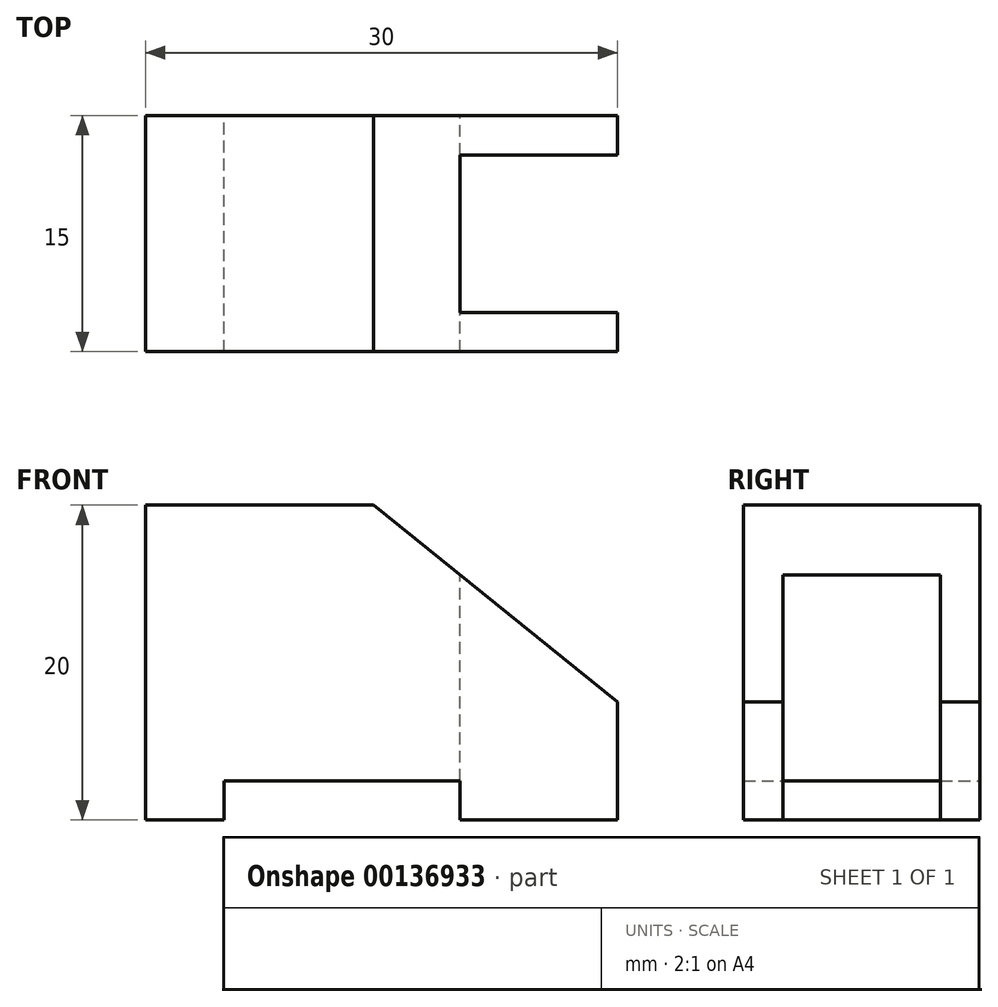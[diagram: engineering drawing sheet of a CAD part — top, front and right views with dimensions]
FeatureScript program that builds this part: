
annotation { "Feature Type Name" : "Feature", "Feature Type Description" : "" }
export const myFeature = defineFeature(function(context is Context, id is Id, definition is map)
    precondition{}
    {
        {
            var Q0;
            Q0=qCreatedBy(makeId("Front.planeOp"),FACE);
            var sketch = newSketch(context, id + "F0", { "sketchPlane" : qUnion([Q0])});
            skLineSegment(sketch, "E0.bottom", {"start": v(0, 0) * mm, "end": v(30, 0) * mm});
            skLineSegment(sketch, "E0.top", {"start": v(0, 20) * mm, "end": v(30, 20) * mm});
            skLineSegment(sketch, "E0.left", {"start": v(0, 0) * mm, "end": v(0, 20) * mm});
            skLineSegment(sketch, "E0.right", {"start": v(30, 0) * mm, "end": v(30, 20) * mm});
            skLineSegment(sketch, "E1", {"start": v(14.5, 20) * mm, "end": v(30, 7.5) * mm});
            skLineSegment(sketch, "E2.bottom", {"start": v(5, 0) * mm, "end": v(20, 0) * mm});
            skLineSegment(sketch, "E2.top", {"start": v(5, 2.5) * mm, "end": v(20, 2.5) * mm});
            skLineSegment(sketch, "E2.left", {"start": v(5, 0) * mm, "end": v(5, 2.5) * mm});
            skLineSegment(sketch, "E2.right", {"start": v(20, 0) * mm, "end": v(20, 2.5) * mm});
            skSolve(sketch);
        }
        {
            var Q0;
            {var subQ0=sQuery(id+"F0.wireOp",EDGE,"E0.left");Q0=makeQuery(id+"F0.imprint","IMPRINT",FACE,{"disambiguationData":[TD([[makeQuery(id+"F0.imprint","IMPRINT",EDGE,{"derivedFrom":subQ0}),-1.0]])]});}
            extrude(context, id + "F1", {"entities" : qUnion([Q0]), "endBound" : BoundingType.SYMMETRIC, "depth" : 15 * mm});
        }
        {
            var Q0;
            Q0=makeQuery(id+"F1.opExtrude","SWEPT_FACE",FACE,{"disambiguationData":[OSD([sQuery(id+"F0.wireOp",EDGE,"E0.top")])]});
            var sketch = newSketch(context, id + "F2", { "sketchPlane" : qUnion([Q0])});
            skLineSegment(sketch, "E3.bottom", {"start": v(20, -5) * mm, "end": v(30, -5) * mm});
            skLineSegment(sketch, "E3.top", {"start": v(20, 5) * mm, "end": v(30, 5) * mm});
            skLineSegment(sketch, "E3.left", {"start": v(20, -5) * mm, "end": v(20, 5) * mm});
            skLineSegment(sketch, "E3.right", {"start": v(30, -5) * mm, "end": v(30, 5) * mm});
            skSolve(sketch);
        }
        {
            var Q0;
            Q0=makeQuery(id+"F2.imprint","IMPRINT",FACE,{"disambiguationData":[TD([[makeQuery(id+"F2.imprint","IMPRINT",EDGE,{"derivedFrom":sQuery(id+"F2.wireOp",EDGE,"E3.bottom")}),1.0]])]});
            extrude(context, id + "F3", {"entities" : qUnion([Q0]), "operationType" : NewBodyOperationType.REMOVE, "endBound" : BoundingType.THROUGH_ALL, "oppositeDirection" : true, "depth" : 25 * mm});
        }
    });
